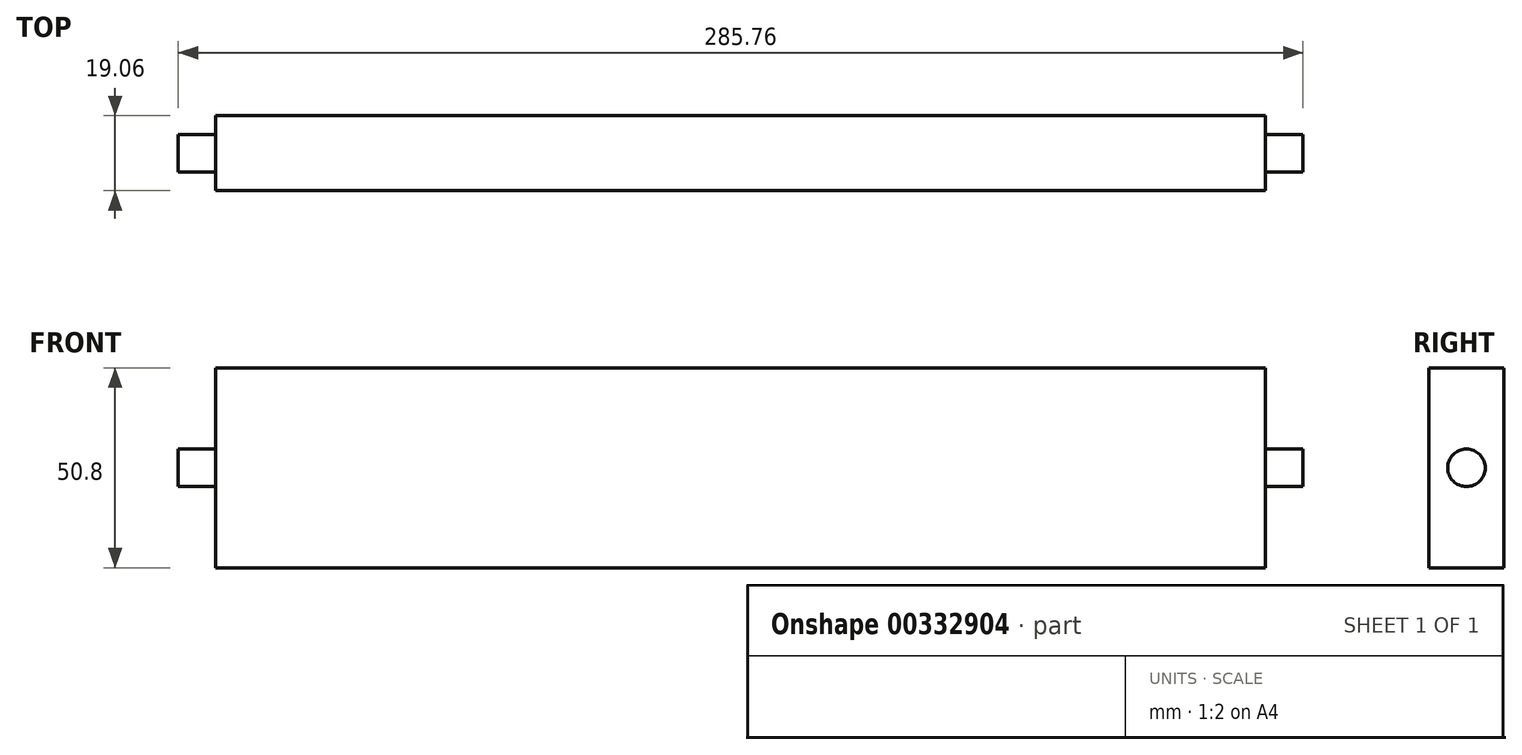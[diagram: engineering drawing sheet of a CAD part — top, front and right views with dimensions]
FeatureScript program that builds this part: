
annotation { "Feature Type Name" : "Feature", "Feature Type Description" : "" }
export const myFeature = defineFeature(function(context is Context, id is Id, definition is map)
    precondition{}
    {
        {
            var Q0;
            Q0=qCreatedBy(makeId("Top.planeOp"),FACE);
            var sketch = newSketch(context, id + "F0", { "sketchPlane" : qUnion([Q0])});
            skLineSegment(sketch, "E0.bottom", {"start": v(-133.35, -9.53) * mm, "end": v(133.35, -9.53) * mm});
            skLineSegment(sketch, "E0.top", {"start": v(-133.35, 9.53) * mm, "end": v(133.35, 9.53) * mm});
            skLineSegment(sketch, "E0.left", {"start": v(-133.35, -9.53) * mm, "end": v(-133.35, 9.52) * mm});
            skLineSegment(sketch, "E0.right", {"start": v(133.35, -9.53) * mm, "end": v(133.35, 9.52) * mm});
            skPoint(sketch, "E0.middle", {"position": v(0, 0) * mm});
            skSolve(sketch);
        }
        {
            var Q0;
            Q0 = qSketchRegion(id + "F0", true);
            extrude(context, id + "F1", {"entities" : qUnion([Q0]), "depth" : 50.8 * mm});
        }
        {
            var Q0;
            Q0=qCreatedBy(makeId("Right.planeOp"),FACE);
            cPlane(context, id + "F2", {"entities" : qUnion([Q0]), "cplaneType" : CPlaneType.OFFSET, "offset" : 133.35 * mm, "width" : 152.4 * mm, "height" : 152.4 * mm});
        }
        {
            var Q0;
            Q0=qCreatedBy(id+"F2.planeOp",FACE);
            var sketch = newSketch(context, id + "F3", { "sketchPlane" : qUnion([Q0])});
            skCircle(sketch, "E1", {"center": v(0, 25.4) * mm, "radius": 4.76 * mm});
            skSolve(sketch);
        }
        {
            var Q0;
            Q0 = qSketchRegion(id + "F3", true);
            extrude(context, id + "F4", {"entities" : qUnion([Q0]), "operationType" : NewBodyOperationType.ADD, "depth" : 9.52 * mm});
        }
        {
            var Q0;
            Q0=qCreatedBy(makeId("Right.planeOp"),FACE);
            cPlane(context, id + "F5", {"entities" : qUnion([Q0]), "cplaneType" : CPlaneType.OFFSET, "offset" : 133.35 * mm, "oppositeDirection" : true, "width" : 152.4 * mm, "height" : 152.4 * mm});
        }
        {
            var Q0;
            Q0=qCreatedBy(id+"F5.planeOp",FACE);
            var sketch = newSketch(context, id + "F6", { "sketchPlane" : qUnion([Q0])});
            skCircle(sketch, "E2", {"center": v(0, 25.42) * mm, "radius": 4.76 * mm});
            skSolve(sketch);
        }
        {
            var Q0;
            Q0 = qSketchRegion(id + "F6", true);
            extrude(context, id + "F7", {"entities" : qUnion([Q0]), "operationType" : NewBodyOperationType.ADD, "oppositeDirection" : true, "depth" : 9.52 * mm});
        }
    });
